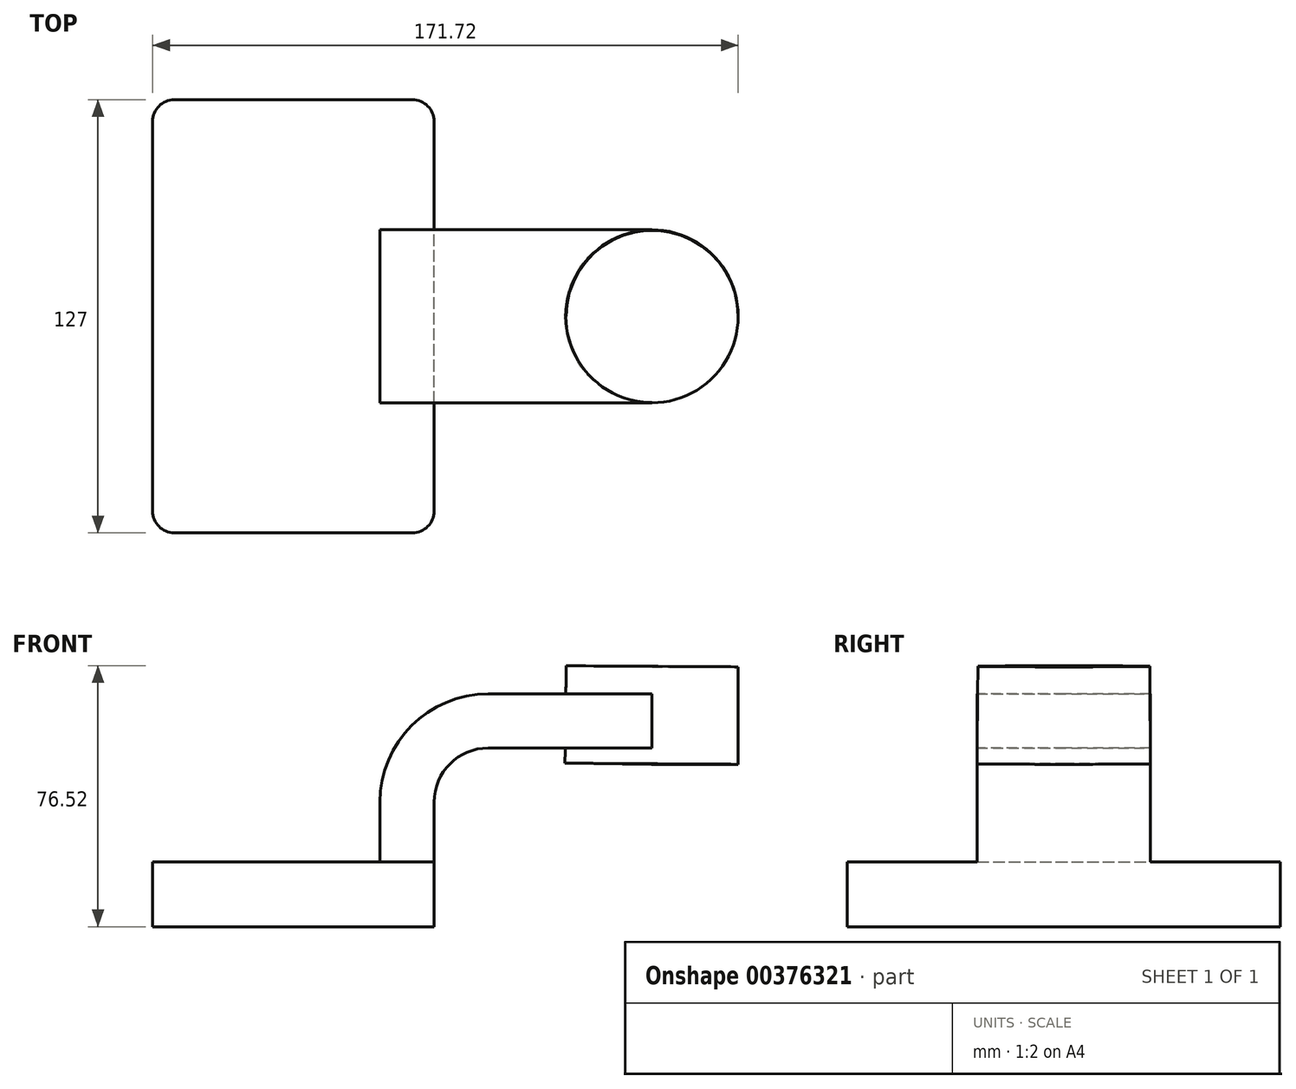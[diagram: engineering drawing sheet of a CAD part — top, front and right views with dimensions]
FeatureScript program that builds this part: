
annotation { "Feature Type Name" : "Feature", "Feature Type Description" : "" }
export const myFeature = defineFeature(function(context is Context, id is Id, definition is map)
    precondition{}
    {
        {
            var Q0;
            Q0=qCreatedBy(makeId("Front.planeOp"),FACE);
            var sketch = newSketch(context, id + "F0", { "sketchPlane" : qUnion([Q0])});
            skLineSegment(sketch, "E0.bottom", {"start": v(41.28, -9.52) * mm, "end": v(-41.28, -9.53) * mm});
            skLineSegment(sketch, "E0.top", {"start": v(41.28, 9.53) * mm, "end": v(-41.28, 9.53) * mm});
            skLineSegment(sketch, "E0.left", {"start": v(41.28, -9.52) * mm, "end": v(41.28, 9.53) * mm});
            skLineSegment(sketch, "E0.right", {"start": v(-41.28, -9.53) * mm, "end": v(-41.28, 9.53) * mm});
            skPoint(sketch, "E0.middle", {"position": v(0, 0) * mm});
            skLineSegment(sketch, "E1.bottom", {"start": v(79.65, 38.1) * mm, "end": v(130.45, 38.1) * mm});
            skLineSegment(sketch, "E1.top", {"start": v(79.65, 66.68) * mm, "end": v(130.45, 66.68) * mm});
            skLineSegment(sketch, "E1.left", {"start": v(79.65, 38.1) * mm, "end": v(79.65, 66.68) * mm});
            skLineSegment(sketch, "E1.right", {"start": v(130.45, 38.1) * mm, "end": v(130.45, 66.68) * mm});
            skPoint(sketch, "E1.middle", {"position": v(105.05, 52.39) * mm});
            skLineSegment(sketch, "E2", {"start": v(41.28, 9.53) * mm, "end": v(41.28, 27) * mm});
            skArc(sketch, "E3", {"start": v(41.27, 27) * mm, "mid": v(45.92, 38.23) * mm, "end": v(57.15, 42.88) * mm});
            skLineSegment(sketch, "E4", {"start": v(57.15, 42.88) * mm, "end": v(105.22, 42.88) * mm});
            skLineSegment(sketch, "E5.0", {"start": v(57.15, 58.75) * mm, "end": v(105.22, 58.75) * mm});
            skArc(sketch, "E5.1", {"start": v(25.4, 27) * mm, "mid": v(34.7, 49.45) * mm, "end": v(57.15, 58.75) * mm});
            skLineSegment(sketch, "E5.2", {"start": v(25.4, 9.53) * mm, "end": v(25.4, 27) * mm});
            skLineSegment(sketch, "E6", {"start": v(105.05, 38.1) * mm, "end": v(105.22, 66.68) * mm});
            skFitSpline(sketch, "E7", {"points": [v(-41.28, 9.53) * mm, v(57.15, 58.75) * mm], "startDerivative": vector(-2.45, 101.52) * mm, "endDerivative": vector(116.85, -0.17) * mm});
            skSolve(sketch);
        }
        {
            var Q0;
            Q0=makeQuery(id+"F0.imprint","IMPRINT",FACE,{"disambiguationData":[TD([[makeQuery(id+"F0.imprint","IMPRINT",EDGE,{"derivedFrom":sQuery(id+"F0.wireOp",EDGE,"E0.bottom")}),-1.0]])]});
            extrude(context, id + "F1", {"entities" : qUnion([Q0]), "endBound" : BoundingType.SYMMETRIC, "depth" : 127 * mm});
        }
        {
            var Q0;
            {var subQ1=sQuery(id+"F0.wireOp",EDGE,"E2");Q0=makeQuery(id+"F0.imprint","IMPRINT",FACE,{"disambiguationData":[TD([[makeQuery(id+"F0.imprint","IMPRINT",EDGE,{"derivedFrom":subQ1}),1.0]])]});}
            extrude(context, id + "F2", {"entities" : qUnion([Q0]), "operationType" : NewBodyOperationType.ADD, "endBound" : BoundingType.SYMMETRIC, "depth" : 50.8 * mm});
        }
        {
            var Q0;
            Q0=makeQuery(id+"F0.imprint","IMPRINT",FACE,{"disambiguationData":[TD([[makeQuery(id+"F0.imprint","IMPRINT",EDGE,{"derivedFrom":sQuery(id+"F0.wireOp",EDGE,"E5.1")}),1.0]])]});
            extrude(context, id + "F3", {"entities" : qUnion([Q0]), "operationType" : NewBodyOperationType.ADD, "endBound" : BoundingType.SYMMETRIC, "depth" : 15.88 * mm});
        }
        {
            var Q0;
            {var subQ0=sQuery(id+"F0.wireOp",EDGE,"E4");var subQ1=sQuery(id+"F0.wireOp",EDGE,"E1.left");var subQ2=makeQuery(id+"F0.imprint","INTERSECT",VERTEX,{"derivedFrom":[subQ1,subQ0]});Q0=makeQuery(id+"F0.imprint","IMPRINT",FACE,{"disambiguationData":[TD([[makeQuery(id+"F0.imprint","IMPRINT",EDGE,{"disambiguationData":[TD([[subQ2,-1.0]])],"derivedFrom":subQ1}),-1.0]])]});}
            extrude(context, id + "F4", {"entities" : qUnion([Q0]), "operationType" : NewBodyOperationType.ADD, "endBound" : BoundingType.SYMMETRIC, "depth" : 50.8 * mm});
        }
        {
            var Q0;
            {var subQ0=sQuery(id+"F0.wireOp",EDGE,"E1.right");Q0=makeQuery(id+"F0.imprint","IMPRINT",FACE,{"disambiguationData":[TD([[makeQuery(id+"F0.imprint","IMPRINT",EDGE,{"derivedFrom":subQ0}),1.0]])]});}
            var Q1;
            Q1=sQuery(id+"F0.wireOp",EDGE,"E6");
            revolve(context, id + "F5", {"operationType" : NewBodyOperationType.ADD, "entities" : qUnion([Q0]), "axis" : qUnion([Q1]), "revolveType" : RevolveType.FULL});
        }
        {
            var Q0;
            Q0=makeQuery(id+"F1.opExtrude","CAP_EDGE",EDGE,{"disambiguationData":[OSD([sQuery(id+"F0.wireOp",EDGE,"E0.right")])],"isStart":false});
            var Q1;
            Q1=makeQuery(id+"F1.opExtrude","CAP_EDGE",EDGE,{"disambiguationData":[OSD([sQuery(id+"F0.wireOp",EDGE,"E0.left")])],"isStart":false});
            var Q2;
            Q2=makeQuery(id+"F1.opExtrude","CAP_EDGE",EDGE,{"disambiguationData":[OSD([sQuery(id+"F0.wireOp",EDGE,"E0.left")])],"isStart":true});
            var Q3;
            Q3=makeQuery(id+"F1.opExtrude","CAP_EDGE",EDGE,{"disambiguationData":[OSD([sQuery(id+"F0.wireOp",EDGE,"E0.right")])],"isStart":true});
            fillet(context, id + "F6", {"entities" : qUnion([Q0, Q1, Q2, Q3]), "radius" : 6.35 * mm, "tangentPropagation" : true, "allowEdgeOverflow" : false});
        }
        {
            var Q0;
            Q0=qCreatedBy(makeId("Top.planeOp"),FACE);
            var Q1;
            Q1=sQuery(id+"F0.wireOp",VERTEX,"E6.end");
            cPlane(context, id + "F7", {"entities" : qUnion([Q0, Q1]), "cplaneType" : CPlaneType.PLANE_POINT, "offset" : 25.4 * mm, "width" : 152.4 * mm, "height" : 152.4 * mm});
        }
    });
